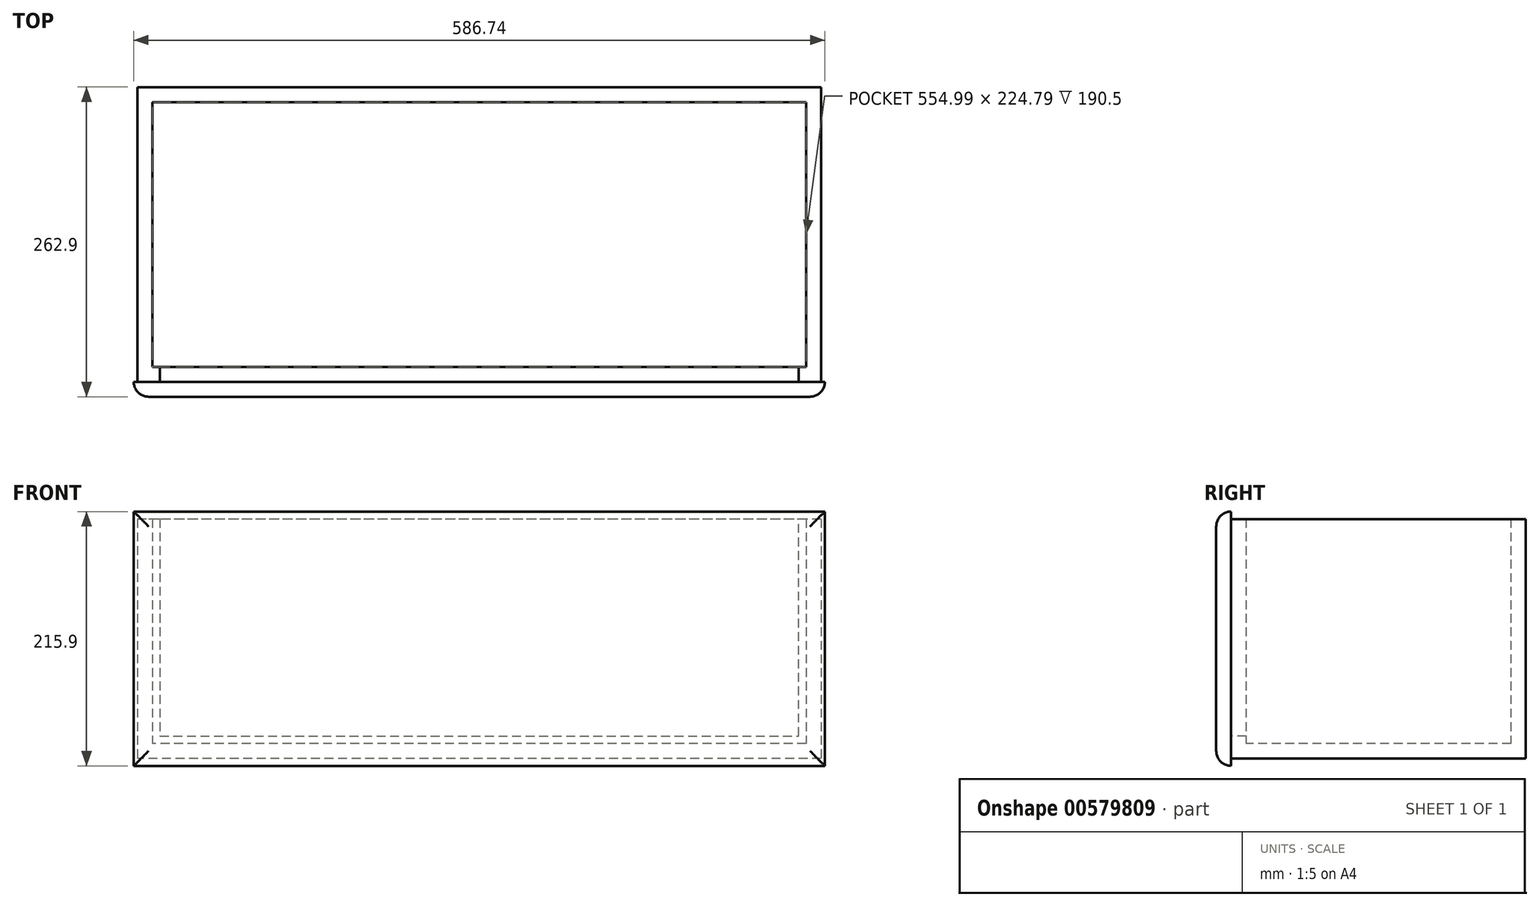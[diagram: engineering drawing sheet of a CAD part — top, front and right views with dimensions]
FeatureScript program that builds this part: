
annotation { "Feature Type Name" : "Feature", "Feature Type Description" : "" }
export const myFeature = defineFeature(function(context is Context, id is Id, definition is map)
    precondition{}
    {
        {
            var Q0;
            Q0=qCreatedBy(makeId("Top.planeOp"),FACE);
            var sketch = newSketch(context, id + "F0", { "sketchPlane" : qUnion([Q0])});
            skLineSegment(sketch, "E0.bottom", {"start": v(290.2, 125.1) * mm, "end": v(-290.2, 125.1) * mm});
            skLineSegment(sketch, "E0.top", {"start": v(290.2, -125.1) * mm, "end": v(-290.2, -125.1) * mm});
            skLineSegment(sketch, "E0.left", {"start": v(290.2, 125.1) * mm, "end": v(290.2, -125.1) * mm});
            skLineSegment(sketch, "E0.right", {"start": v(-290.2, 125.1) * mm, "end": v(-290.2, -125.1) * mm});
            skPoint(sketch, "E0.middle", {"position": v(0, 0) * mm});
            skSolve(sketch);
        }
        {
            var Q0;
            Q0=makeQuery(id+"F0.imprint","IMPRINT",FACE,{"disambiguationData":[TD([[makeQuery(id+"F0.imprint","IMPRINT",EDGE,{"derivedFrom":sQuery(id+"F0.wireOp",EDGE,"E0.bottom")}),1.0]])]});
            extrude(context, id + "F1", {"entities" : qUnion([Q0]), "endBound" : BoundingType.SYMMETRIC, "depth" : 203.2 * mm, "offsetDistance" : 25.4 * mm});
        }
        {
            var Q0;
            Q0=makeQuery(id+"F1.opExtrude","CAP_FACE",FACE,{"disambiguationData":[OSD([sQuery(id+"F0.wireOp",EDGE,"E0.bottom"),sQuery(id+"F0.wireOp",EDGE,"E0.top"),sQuery(id+"F0.wireOp",EDGE,"E0.left"),sQuery(id+"F0.wireOp",EDGE,"E0.right")])],"isStart":false});
            shell(context, id + "F2", {"entities" : qUnion([Q0]), "thickness" : 12.7 * mm});
        }
        {
            var Q0;
            Q0=makeQuery(id+"F1.opExtrude","SWEPT_FACE",FACE,{"disambiguationData":[OSD([sQuery(id+"F0.wireOp",EDGE,"E0.top")])]});
            var sketch = newSketch(context, id + "F3", { "sketchPlane" : qUnion([Q0])});
            skLineSegment(sketch, "E1", {"start": v(-271.15, 101.6) * mm, "end": v(-271.15, -82.55) * mm});
            skLineSegment(sketch, "E2", {"start": v(-271.15, -82.55) * mm, "end": v(271.15, -82.55) * mm});
            skLineSegment(sketch, "E3", {"start": v(271.15, -82.55) * mm, "end": v(271.15, 101.6) * mm});
            skSolve(sketch);
        }
        {
            var Q0;
            {var subQ0=sQuery(id+"F3.wireOp",EDGE,"E1");Q0=makeQuery(id+"F3.imprint","IMPRINT",FACE,{"disambiguationData":[TD([[makeQuery(id+"F3.imprint","IMPRINT",EDGE,{"derivedFrom":subQ0}),1.0]])]});}
            extrude(context, id + "F4", {"entities" : qUnion([Q0]), "operationType" : NewBodyOperationType.REMOVE, "oppositeDirection" : true, "depth" : 25.4 * mm, "offsetDistance" : 25.4 * mm});
        }
        {
            var Q0;
            Q0=makeQuery(id+"F1.opExtrude","SWEPT_FACE",FACE,{"disambiguationData":[OSD([sQuery(id+"F0.wireOp",EDGE,"E0.top")])]});
            var sketch = newSketch(context, id + "F5", { "sketchPlane" : qUnion([Q0])});
            skLineSegment(sketch, "E4.bottom", {"start": v(293.37, 107.95) * mm, "end": v(-293.37, 107.95) * mm});
            skLineSegment(sketch, "E4.top", {"start": v(293.37, -107.95) * mm, "end": v(-293.37, -107.95) * mm});
            skLineSegment(sketch, "E4.left", {"start": v(293.37, 107.95) * mm, "end": v(293.37, -107.95) * mm});
            skLineSegment(sketch, "E4.right", {"start": v(-293.37, 107.95) * mm, "end": v(-293.37, -107.95) * mm});
            skPoint(sketch, "E4.middle", {"position": v(0, 0) * mm});
            skSolve(sketch);
        }
        {
            var Q0;
            Q0=makeQuery(id+"F5.imprint","IMPRINT",FACE,{"disambiguationData":[TD([[makeQuery(id+"F5.imprint","IMPRINT",EDGE,{"derivedFrom":sQuery(id+"F5.wireOp",EDGE,"E4.bottom")}),1.0]])]});
            var Q1;
            {var subQ1=sQuery(id+"F0.wireOp",EDGE,"E0.top");Q1=makeQuery(id+"F5.imprint","IMPRINT",FACE,{"disambiguationData":[TD([[makeQuery(id+"F5.imprint","IMPRINT",EDGE,{"derivedFrom":makeQuery(id+"F1.opExtrude","CAP_EDGE",EDGE,{"disambiguationData":[OSD([subQ1])],"isStart":true})}),-1.0]])]});}
            extrude(context, id + "F6", {"entities" : qUnion([Q0, Q1]), "operationType" : NewBodyOperationType.ADD, "depth" : 12.7 * mm, "offsetDistance" : 25.4 * mm});
        }
        {
            var Q0;
            Q0=makeQuery(id+"F6.opExtrude","CAP_EDGE",EDGE,{"disambiguationData":[OSD([sQuery(id+"F5.wireOp",EDGE,"E4.bottom")])],"isStart":false});
            var Q1;
            Q1=makeQuery(id+"F6.opExtrude","CAP_EDGE",EDGE,{"disambiguationData":[OSD([sQuery(id+"F5.wireOp",EDGE,"E4.right")])],"isStart":false});
            var Q2;
            Q2=makeQuery(id+"F6.opExtrude","CAP_EDGE",EDGE,{"disambiguationData":[OSD([sQuery(id+"F5.wireOp",EDGE,"E4.top")])],"isStart":false});
            var Q3;
            Q3=makeQuery(id+"F6.opExtrude","CAP_EDGE",EDGE,{"disambiguationData":[OSD([sQuery(id+"F5.wireOp",EDGE,"E4.left")])],"isStart":false});
            fillet(context, id + "F7", {"entities" : qUnion([Q0, Q1, Q2, Q3]), "radius" : 12.7 * mm, "tangentPropagation" : true, "allowEdgeOverflow" : false});
        }
    });
